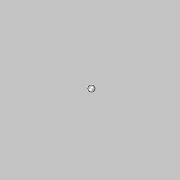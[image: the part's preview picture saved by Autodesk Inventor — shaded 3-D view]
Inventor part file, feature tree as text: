
AUTODESK INVENTOR PART (.ipt)
format: ipt  version: 2017 (Build 210142000, 142)  size: 112,640 bytes
history: native  units: mm
features: extrude x4, sketch x4, fillet x1, projected_geometry x1
ambient origin geometry x8: Origin, YZ Plane, XZ Plane, XY Plane, X Axis, Y Axis, Z Axis, Center Point
bodies: Solid1 (feature_tree)
feature tree (10):
  extrude  "Extrusion1"  Depth=75.0mm
  extrude  "Extrusion2"  Depth=35.0mm
  extrude  "Extrusion3"  Depth=60.0mm
  extrude  "Extrusion240V1"  Depth=44.0mm TaperAngle=0.0deg
  fillet  "Fillet240V1"  [1 undecoded]
  sketch  "Sketch1"  dims[d0=75.0mm d1=75.0mm]
  sketch  "Sketch2"  dims[d2=50.0mm d3=0.0mm d4=35.0mm]
  sketch  "Sketch3"  dims[d5=34.0mm d6=1.745329mm d7=60.0mm]
  projected_geometry  "Projected Loop1"
  sketch  "Sketch7"  dims[d8=5.0mm d9=44.0mm d10=0.0mm d22=0.0mm d28=2.5mm d29=10.0mm d30=0.0mm d31=5.0mm]
note: 1 required parameter value undecoded (feature->parameter linkage not recoverable at this tier; creation-order binding heuristic only, values carry confidence <= 0.55)
